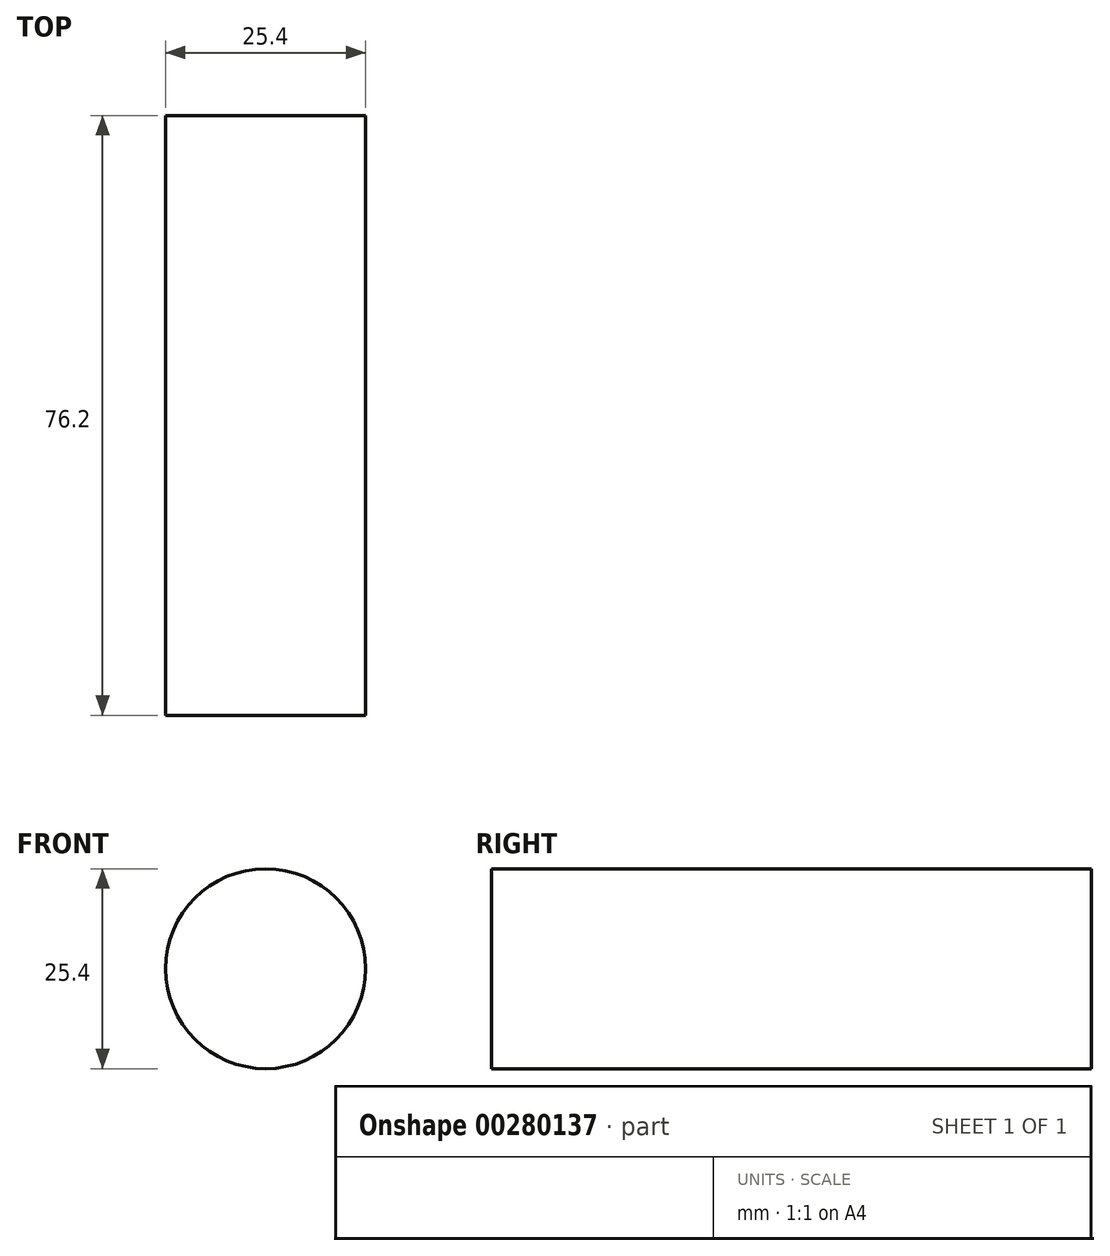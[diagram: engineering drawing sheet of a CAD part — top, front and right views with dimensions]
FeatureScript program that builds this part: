
annotation { "Feature Type Name" : "Feature", "Feature Type Description" : "" }
export const myFeature = defineFeature(function(context is Context, id is Id, definition is map)
    precondition{}
    {
        {
            var Q0;
            Q0=qCreatedBy(makeId("Front.planeOp"),FACE);
            var sketch = newSketch(context, id + "F0", { "sketchPlane" : qUnion([Q0])});
            skCircle(sketch, "E0", {"center": v(-45.45, 30.74) * mm, "radius": 12.7 * mm});
            skSolve(sketch);
        }
        {
            var Q0;
            Q0 = qSketchRegion(id + "F0", true);
            extrude(context, id + "F1", {"entities" : qUnion([Q0]), "depth" : 76.2 * mm});
        }
    });
